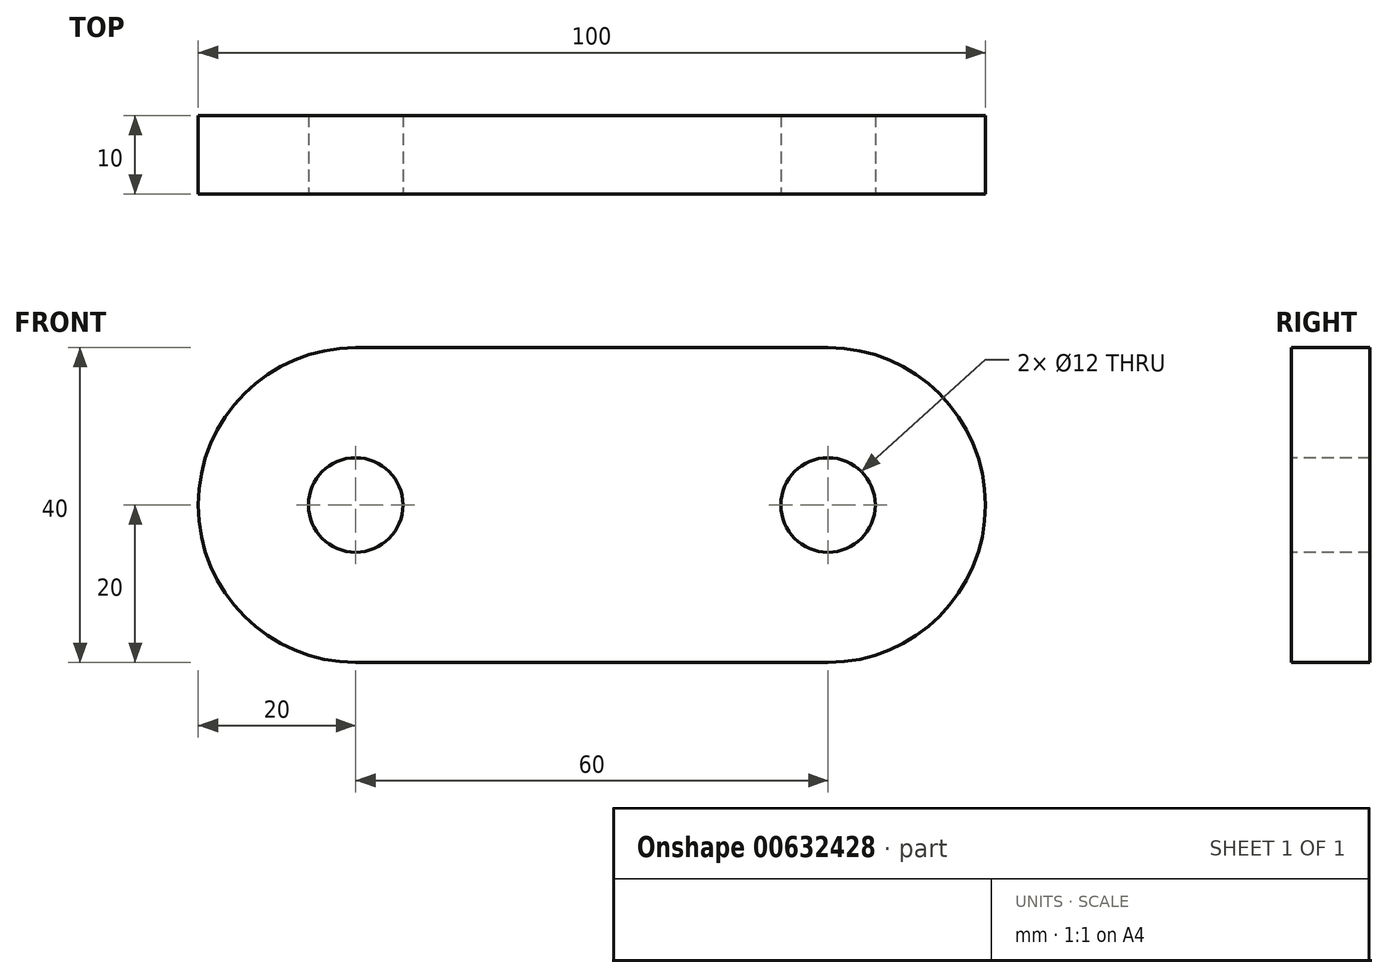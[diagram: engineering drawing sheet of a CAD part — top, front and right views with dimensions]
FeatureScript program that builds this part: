
annotation { "Feature Type Name" : "Feature", "Feature Type Description" : "" }
export const myFeature = defineFeature(function(context is Context, id is Id, definition is map)
    precondition{}
    {
        {
            var Q0;
            Q0=qCreatedBy(makeId("Front.planeOp"),FACE);
            var sketch = newSketch(context, id + "F0", { "sketchPlane" : qUnion([Q0])});
            skLineSegment(sketch, "E0.bottom", {"start": v(0, 0) * mm, "end": v(60, 0) * mm});
            skLineSegment(sketch, "E0.top", {"start": v(0, 40) * mm, "end": v(60, 40) * mm});
            skArc(sketch, "E1", {"start": v(60, 0) * mm, "mid": v(80, 20) * mm, "end": v(60, 40) * mm});
            skArc(sketch, "E2", {"start": v(0, 40) * mm, "mid": v(-20, 20) * mm, "end": v(0, 0) * mm});
            skLineSegment(sketch, "E3", {"start": v(0, 40) * mm, "end": v(0, 0) * mm, "construction": true});
            skLineSegment(sketch, "E4", {"start": v(60, 40) * mm, "end": v(60, 0) * mm, "construction": true});
            skLineSegment(sketch, "E5", {"start": v(-20, 20) * mm, "end": v(80, 20) * mm, "construction": true});
            skSolve(sketch);
        }
        {
            var Q0;
            Q0=makeQuery(id+"F0.imprint","IMPRINT",FACE,{"disambiguationData":[TD([[makeQuery(id+"F0.imprint","IMPRINT",EDGE,{"derivedFrom":sQuery(id+"F0.wireOp",EDGE,"E0.bottom")}),1.0]])]});
            extrude(context, id + "F1", {"entities" : qUnion([Q0]), "depth" : 10 * mm, "offsetDistance" : 25 * mm});
        }
        {
            var Q0;
            Q0=sQuery(id+"F0.wireOp",VERTEX,"E2.center");
            var Q1;
            Q1=sQuery(id+"F0.wireOp",VERTEX,"E1.center");
            var Q2;
            Q2=makeQuery(id+"F1.opExtrude","SWEPT_BODY",BODY,{"disambiguationData":[OSD([sQuery(id+"F0.wireOp",EDGE,"E0.bottom"),sQuery(id+"F0.wireOp",EDGE,"E0.top"),sQuery(id+"F0.wireOp",EDGE,"E1"),sQuery(id+"F0.wireOp",EDGE,"E2")])]});
            hole(context, id + "F2", {"style" : HoleStyle.SIMPLE, "endStyle" : HoleEndStyle.THROUGH, "oppositeDirection" : true, "standardTappedOrClearance" : lookupTablePath({ "standard" : "ISO", "size" : "12", "type" : "Drilled" }), "standardBlindInLast" : lookupTablePath({ "standard" : "ISO", "size" : "12", "type" : "Drilled" }), "holeDiameter" : 12 * mm, "majorDiameter" : 12 * mm, "isTappedThrough" : true, "tappedDepth" : 12 * mm, "tapClearance" : 3, "startFromSketch" : true, "locations" : qUnion([Q0, Q1]), "scope" : qUnion([Q2])});
        }
    });
